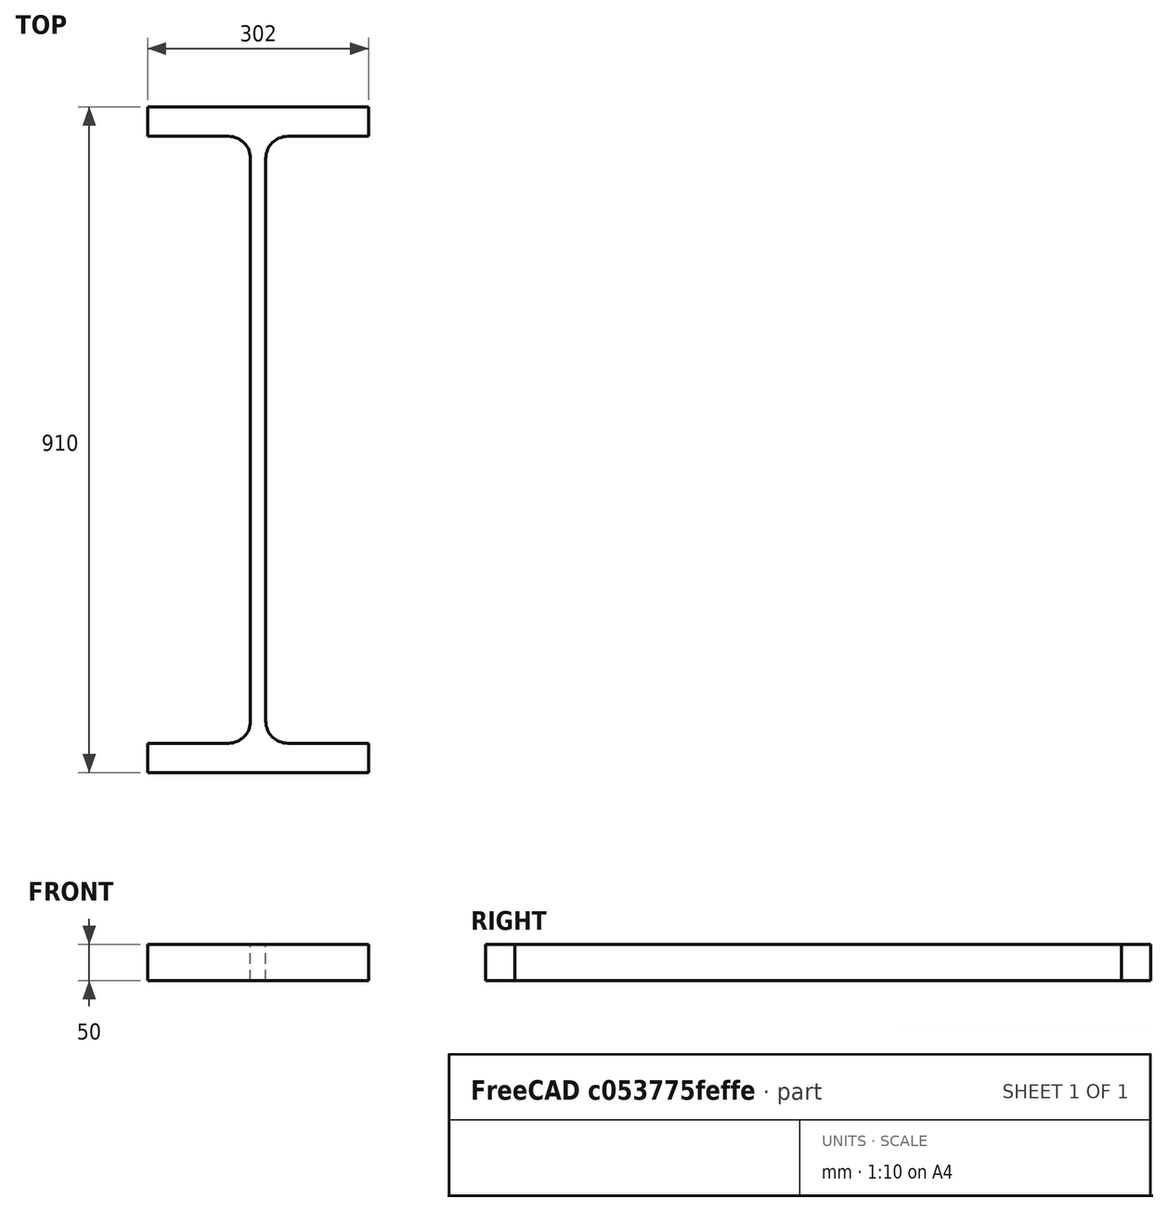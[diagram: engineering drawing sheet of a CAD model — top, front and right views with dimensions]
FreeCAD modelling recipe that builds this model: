
FCSTD DOCUMENT  (FreeCAD 0.15R4671 (Git))
Label: HE-M-Profile 900 DIN1025-4 S235JR
License: All rights reserved
LicenseURL: http://en.wikipedia.org/wiki/All_rights_reserved
objects: Sketcher::SketchObject×1, Part::Extrusion×1
note: 2 computed .brp shape members not serialized (recipe doc carries the construction recipe); baked Part::Feature solids carry a one-line shape summary decoded from their .brp

FEATURE [Sketcher::SketchObject] Sketch
  sketch-geometry (16):
    g0: LineSegment StartX=10.5 StartY=-385 StartZ=0 EndX=10.5 EndY=385 EndZ=0
    g1: LineSegment StartX=40.5 StartY=415 StartZ=0 EndX=151 EndY=415 EndZ=0
    g2: LineSegment StartX=151 StartY=415 StartZ=0 EndX=151 EndY=455 EndZ=0
    g3: LineSegment StartX=151 StartY=455 StartZ=0 EndX=-151 EndY=455 EndZ=0
    g4: LineSegment StartX=-151 StartY=455 StartZ=0 EndX=-151 EndY=415 EndZ=0
    g5: LineSegment StartX=-151 StartY=415 StartZ=0 EndX=-40.5 EndY=415 EndZ=0
    g6: LineSegment StartX=-10.5 StartY=385 StartZ=0 EndX=-10.5 EndY=-385 EndZ=0
    g7: LineSegment StartX=-40.5 StartY=-415 StartZ=0 EndX=-151 EndY=-415 EndZ=0
    g8: LineSegment StartX=-151 StartY=-415 StartZ=0 EndX=-151 EndY=-455 EndZ=0
    g9: LineSegment StartX=-151 StartY=-455 StartZ=0 EndX=151 EndY=-455 EndZ=0
    g10: LineSegment StartX=151 StartY=-455 StartZ=0 EndX=151 EndY=-415 EndZ=0
    g11: LineSegment StartX=151 StartY=-415 StartZ=0 EndX=40.5 EndY=-415 EndZ=0
    g12: ArcOfCircle CenterX=40.5 CenterY=385 CenterZ=0 NormalX=0 NormalY=0 NormalZ=1 Radius=30 StartAngle=1.5708 EndAngle=3.14159
    g13: ArcOfCircle CenterX=40.5 CenterY=-385 CenterZ=0 NormalX=0 NormalY=0 NormalZ=1 Radius=30 StartAngle=3.14159 EndAngle=4.71239
    g14: ArcOfCircle CenterX=-40.5 CenterY=385 CenterZ=0 NormalX=0 NormalY=0 NormalZ=1 Radius=30 StartAngle=0 EndAngle=1.5708
    g15: ArcOfCircle CenterX=-40.5 CenterY=-385 CenterZ=0 NormalX=0 NormalY=0 NormalZ=1 Radius=30 StartAngle=4.71239 EndAngle=6.28319
  constraints (42):
    c: Vertical(g0)
    c: Coincident(g2,g1)
    c: Vertical(g2)
    c: Coincident(g3,g2)
    c: Coincident(g4,g3)
    c: Vertical(g4)
    c: Coincident(g5,g4)
    c: Horizontal(g5)
    c: Vertical(g6)
    c: Horizontal(g7)
    c: Coincident(g8,g7)
    c: Vertical(g8)
    c: Coincident(g9,g8)
    c: Horizontal(g9)
    c: Coincident(g10,g9)
    c: Vertical(g10)
    c: Coincident(g11,g10)
    c: Horizontal(g11)
    c: Tangent(g1,g12) = 1.5708
    c: Tangent(g0,g12) = 1.5708
    c: Tangent(g0,g13) = 1.5708
    c: Tangent(g11,g13) = 1.5708
    c: Tangent(g5,g14) = 1.5708
    c: Tangent(g6,g14) = 1.5708
    c: Tangent(g6,g15) = 1.5708
    c: Tangent(g7,g15) = 1.5708
    c: Equal(g3,g9)
    c: Equal(g2,g4)
    c: Equal(g4,g8)
    c: Equal(g8,g10)
    c: Equal(g12,g14)
    c: Equal(g14,g15)
    c: Equal(g15,g13)
    c: Symmetric(g2,g3,g-2)
    c: Symmetric(g9,g8,g-2)
    c: Symmetric(g0,g6,g-2)
    c: Symmetric(g2,g9,g-1)
    c: DistanceY(g2,g9) = -910
    c: DistanceX(g3) = -302
    c: DistanceX(g0,g6) = -21
    c: DistanceY(g2) = 40
    c: Radius(g12) = 30
FEATURE [Part::Extrusion] Extrude  label="HE-M-Profile 900 DIN1025-4 S235JR"
  Base = -> Sketch
  Dir = (0,0,50)
  Solid = true
